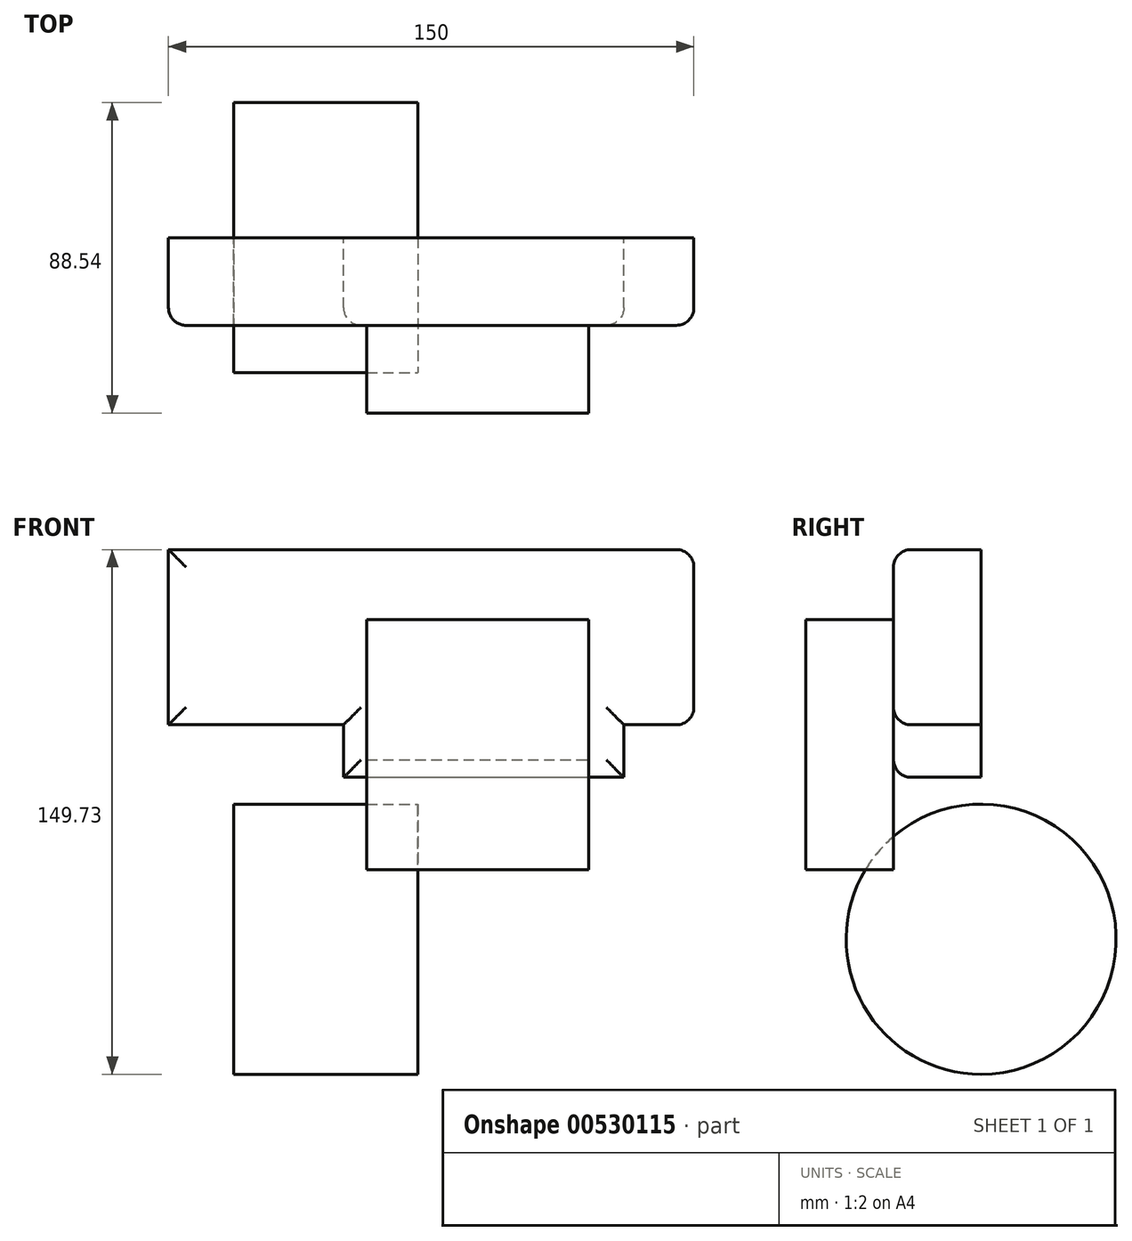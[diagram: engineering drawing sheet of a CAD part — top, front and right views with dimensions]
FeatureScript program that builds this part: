
annotation { "Feature Type Name" : "Feature", "Feature Type Description" : "" }
export const myFeature = defineFeature(function(context is Context, id is Id, definition is map)
    precondition{}
    {
        {
            var Q0;
            Q0=qCreatedBy(makeId("Front.planeOp"),FACE);
            var sketch = newSketch(context, id + "F0", { "sketchPlane" : qUnion([Q0])});
            skLineSegment(sketch, "E0.bottom", {"start": v(0, 0) * mm, "end": v(150, 0) * mm});
            skLineSegment(sketch, "E0.top", {"start": v(0, -50) * mm, "end": v(150, -50) * mm});
            skLineSegment(sketch, "E0.left", {"start": v(0, 0) * mm, "end": v(0, -50) * mm});
            skLineSegment(sketch, "E0.right", {"start": v(150, 0) * mm, "end": v(150, -50) * mm});
            skLineSegment(sketch, "E1.bottom", {"start": v(50, -25) * mm, "end": v(130, -25) * mm});
            skLineSegment(sketch, "E1.top", {"start": v(50, -65) * mm, "end": v(130, -65) * mm});
            skLineSegment(sketch, "E1.left", {"start": v(50, -25) * mm, "end": v(50, -65) * mm});
            skLineSegment(sketch, "E1.right", {"start": v(130, -25) * mm, "end": v(130, -65) * mm});
            skCircle(sketch, "E2", {"center": v(32.45, -86.92) * mm, "radius": 24.07 * mm});
            skCircle(sketch, "E3", {"center": v(113.68, -105.17) * mm, "radius": 26.37 * mm});
            skSolve(sketch);
        }
        {
            var Q0;
            {var subQ1=sQuery(id+"F0.wireOp",EDGE,"E0.bottom");Q0=makeQuery(id+"F0.imprint","IMPRINT",FACE,{"disambiguationData":[TD([[makeQuery(id+"F0.imprint","IMPRINT",EDGE,{"derivedFrom":subQ1}),-1.0]])]});}
            var Q1;
            {var subQ0=sQuery(id+"F0.wireOp",EDGE,"E1.top");Q1=makeQuery(id+"F0.imprint","IMPRINT",FACE,{"disambiguationData":[TD([[makeQuery(id+"F0.imprint","IMPRINT",EDGE,{"derivedFrom":subQ0}),1.0]])]});}
            var Q2;
            {var subQ0=sQuery(id+"F0.wireOp",EDGE,"E0.right");var subQ1=sQuery(id+"F0.wireOp",EDGE,"E0.top");var subQ2=makeQuery(id+"F0.imprint","INTERSECT",VERTEX,{"derivedFrom":[subQ1,subQ0]});Q2=makeQuery(id+"F0.imprint","IMPRINT",FACE,{"disambiguationData":[TD([[makeQuery(id+"F0.imprint","IMPRINT",EDGE,{"disambiguationData":[TD([[subQ2,1.0]])],"derivedFrom":subQ1}),1.0]])]});}
            var Q3;
            {var subQ0=sQuery(id+"F0.wireOp",EDGE,"E2");var subQ1=sQuery(id+"F0.wireOp",EDGE,"E0.top");var subQ2=makeQuery(id+"F0.imprint","INTERSECT",VERTEX,{"disambiguationData":[OD(0.0)],"derivedFrom":[subQ1,subQ0]});Q3=makeQuery(id+"F0.imprint","IMPRINT",FACE,{"disambiguationData":[TD([[makeQuery(id+"F0.imprint","IMPRINT",EDGE,{"disambiguationData":[TD([[subQ2,-1.0]])],"derivedFrom":subQ1}),1.0]])]});}
            var Q4;
            {var subQ0=sQuery(id+"F0.wireOp",EDGE,"E3");var subQ1=sQuery(id+"F0.wireOp",EDGE,"E1.top");var subQ2=makeQuery(id+"F0.imprint","INTERSECT",VERTEX,{"disambiguationData":[OD(0.0)],"derivedFrom":[subQ1,subQ0]});Q4=makeQuery(id+"F0.imprint","IMPRINT",FACE,{"disambiguationData":[TD([[makeQuery(id+"F0.imprint","IMPRINT",EDGE,{"disambiguationData":[TD([[subQ2,-1.0]])],"derivedFrom":subQ1}),1.0]])]});}
            var Q5;
            {var subQ5=sQuery(id+"F0.wireOp",EDGE,"E1.bottom");Q5=makeQuery(id+"F0.imprint","IMPRINT",FACE,{"disambiguationData":[TD([[makeQuery(id+"F0.imprint","IMPRINT",EDGE,{"derivedFrom":subQ5}),-1.0]])]});}
            extrude(context, id + "F1", {"entities" : qUnion([Q0, Q1, Q2, Q3, Q4, Q5]), "depth" : 25 * mm, "offsetDistance" : 25 * mm});
        }
        {
            var Q0;
            Q0=makeQuery(id+"F1.opExtrude","CAP_FACE",FACE,{"disambiguationData":[OSD([sQuery(id+"F0.wireOp",EDGE,"E0.bottom"),sQuery(id+"F0.wireOp",EDGE,"E0.top"),sQuery(id+"F0.wireOp",EDGE,"E0.left"),sQuery(id+"F0.wireOp",EDGE,"E0.right"),sQuery(id+"F0.wireOp",EDGE,"E1.bottom"),sQuery(id+"F0.wireOp",EDGE,"E1.top"),sQuery(id+"F0.wireOp",EDGE,"E1.left"),sQuery(id+"F0.wireOp",EDGE,"E1.right")])],"isStart":false});
            fillet(context, id + "F2", {"entities" : qUnion([Q0]), "radius" : 5 * mm, "tangentPropagation" : true, "allowEdgeOverflow" : false});
        }
        {
            var Q0;
            Q0=makeQuery(id+"F1.opExtrude","CAP_FACE",FACE,{"disambiguationData":[OSD([sQuery(id+"F0.wireOp",EDGE,"E0.bottom"),sQuery(id+"F0.wireOp",EDGE,"E0.top"),sQuery(id+"F0.wireOp",EDGE,"E0.left"),sQuery(id+"F0.wireOp",EDGE,"E0.right"),sQuery(id+"F0.wireOp",EDGE,"E1.bottom"),sQuery(id+"F0.wireOp",EDGE,"E1.top"),sQuery(id+"F0.wireOp",EDGE,"E1.left"),sQuery(id+"F0.wireOp",EDGE,"E1.right")])],"isStart":false});
            var sketch = newSketch(context, id + "F3", { "sketchPlane" : qUnion([Q0])});
            skLineSegment(sketch, "E4.bottom", {"start": v(120, -20) * mm, "end": v(20, -20) * mm});
            skLineSegment(sketch, "E4.top", {"start": v(120, -91.36) * mm, "end": v(20, -91.36) * mm});
            skLineSegment(sketch, "E4.left", {"start": v(120, -20) * mm, "end": v(120, -91.36) * mm});
            skLineSegment(sketch, "E4.right", {"start": v(20, -20) * mm, "end": v(20, -91.36) * mm});
            skLineSegment(sketch, "E5", {"start": v(56.65, -20) * mm, "end": v(56.65, -91.36) * mm});
            skSolve(sketch);
        }
        {
            var Q0;
            {var subQ1=sQuery(id+"F3.wireOp",EDGE,"E4.bottom");Q0=makeQuery(id+"F3.imprint","IMPRINT",FACE,{"disambiguationData":[TD([[makeQuery(id+"F3.imprint","IMPRINT",EDGE,{"derivedFrom":subQ1}),1.0]])]});}
            var Q1;
            {var subQ6=sQuery(id+"F3.wireOp",EDGE,"E4.top");Q1=makeQuery(id+"F3.imprint","IMPRINT",FACE,{"disambiguationData":[TD([[makeQuery(id+"F3.imprint","IMPRINT",EDGE,{"derivedFrom":subQ6}),-1.0]])]});}
            extrude(context, id + "F4", {"entities" : qUnion([Q0, Q1]), "operationType" : NewBodyOperationType.ADD, "depth" : 25 * mm, "offsetDistance" : 25 * mm});
        }
        {
            var Q0;
            Q0=qCreatedBy(makeId("Front.planeOp"),FACE);
            var sketch = newSketch(context, id + "F5", { "sketchPlane" : qUnion([Q0])});
            skLineSegment(sketch, "E6.bottom", {"start": v(71.16, -111.2) * mm, "end": v(18.6, -111.2) * mm});
            skLineSegment(sketch, "E6.top", {"start": v(71.16, -149.73) * mm, "end": v(18.6, -149.73) * mm});
            skLineSegment(sketch, "E6.left", {"start": v(71.16, -111.2) * mm, "end": v(71.16, -149.73) * mm});
            skLineSegment(sketch, "E6.right", {"start": v(18.6, -111.2) * mm, "end": v(18.6, -149.73) * mm});
            skSolve(sketch);
        }
        {
            var Q0;
            Q0=makeQuery(id+"F5.imprint","IMPRINT",FACE,{"disambiguationData":[TD([[makeQuery(id+"F5.imprint","IMPRINT",EDGE,{"derivedFrom":sQuery(id+"F5.wireOp",EDGE,"E6.bottom")}),1.0]])]});
            var Q1;
            Q1=sQuery(id+"F5.wireOp",EDGE,"E6.bottom");
            revolve(context, id + "F6", {"entities" : qUnion([Q0]), "axis" : qUnion([Q1]), "revolveType" : RevolveType.FULL});
        }
        {
            var Q0;
            Q0=makeQuery(id+"F1.opExtrude","SWEPT_EDGE",EDGE,{"disambiguationData":[OSD([sQuery(id+"F0.wireOp",EDGE,"E0.right"),sQuery(id+"F0.wireOp",EDGE,"E1.bottom")])]});
            fillet(context, id + "F7", {"entities" : qUnion([Q0]), "radius" : 5 * mm, "tangentPropagation" : true, "allowEdgeOverflow" : false});
        }
    });
